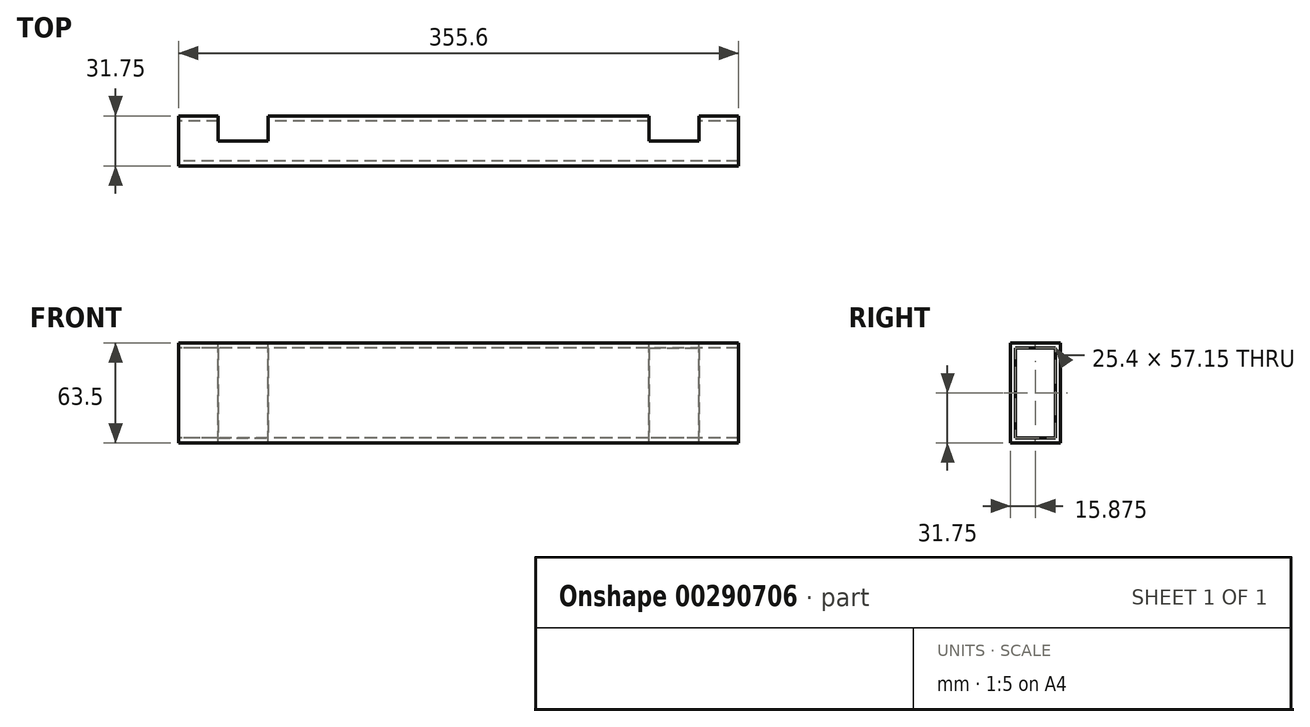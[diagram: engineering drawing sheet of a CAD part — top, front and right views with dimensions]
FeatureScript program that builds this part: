
annotation { "Feature Type Name" : "Feature", "Feature Type Description" : "" }
export const myFeature = defineFeature(function(context is Context, id is Id, definition is map)
    precondition{}
    {
        {
            var Q0;
            Q0=qCreatedBy(makeId("Front.planeOp"),FACE);
            var sketch = newSketch(context, id + "F0", { "sketchPlane" : qUnion([Q0])});
            skLineSegment(sketch, "E0.bottom", {"start": v(0, 0) * mm, "end": v(355.6, 0) * mm});
            skLineSegment(sketch, "E0.top", {"start": v(0, 63.5) * mm, "end": v(355.6, 63.5) * mm});
            skLineSegment(sketch, "E0.left", {"start": v(0, 0) * mm, "end": v(0, 63.5) * mm});
            skLineSegment(sketch, "E0.right", {"start": v(355.6, 0) * mm, "end": v(355.6, 63.5) * mm});
            skSolve(sketch);
        }
        {
            var Q0;
            Q0=makeQuery(id+"F0.imprint","IMPRINT",FACE,{"disambiguationData":[TD([[makeQuery(id+"F0.imprint","IMPRINT",EDGE,{"derivedFrom":sQuery(id+"F0.wireOp",EDGE,"E0.bottom")}),1.0]])]});
            extrude(context, id + "F1", {"entities" : qUnion([Q0]), "depth" : 31.75 * mm});
        }
        {
            var Q0;
            Q0=makeQuery(id+"F1.opExtrude","SWEPT_FACE",FACE,{"disambiguationData":[OSD([sQuery(id+"F0.wireOp",EDGE,"E0.top")])]});
            var sketch = newSketch(context, id + "F2", { "sketchPlane" : qUnion([Q0])});
            skLineSegment(sketch, "E1.bottom", {"start": v(25.19, 0) * mm, "end": v(56.94, 0) * mm});
            skLineSegment(sketch, "E1.top", {"start": v(25.19, -16.02) * mm, "end": v(56.94, -16.02) * mm});
            skLineSegment(sketch, "E1.left", {"start": v(25.19, 0) * mm, "end": v(25.19, -16.02) * mm});
            skLineSegment(sketch, "E1.right", {"start": v(56.94, 0) * mm, "end": v(56.94, -16.02) * mm});
            skLineSegment(sketch, "E2", {"start": v(177.8, 0) * mm, "end": v(177.8, -31.75) * mm, "construction": true});
            skLineSegment(sketch, "E3.MirrorCS", {"start": v(330.41, 0) * mm, "end": v(330.41, -16.02) * mm});
            skLineSegment(sketch, "E4.MirrorCS", {"start": v(330.41, -16.02) * mm, "end": v(298.66, -16.02) * mm});
            skLineSegment(sketch, "E5.MirrorCS", {"start": v(298.66, 0) * mm, "end": v(298.66, -16.02) * mm});
            skLineSegment(sketch, "E6.MirrorCS", {"start": v(330.41, 0) * mm, "end": v(298.66, 0) * mm});
            skSolve(sketch);
        }
        {
            var Q0;
            Q0=makeQuery(id+"F2.imprint","IMPRINT",FACE,{"disambiguationData":[TD([[makeQuery(id+"F2.imprint","IMPRINT",EDGE,{"derivedFrom":sQuery(id+"F2.wireOp",EDGE,"E1.bottom")}),-1.0]])]});
            var Q1;
            Q1=makeQuery(id+"F2.imprint","IMPRINT",FACE,{"disambiguationData":[TD([[makeQuery(id+"F2.imprint","IMPRINT",EDGE,{"derivedFrom":sQuery(id+"F2.wireOp",EDGE,"E3.MirrorCS")}),-1.0]])]});
            extrude(context, id + "F3", {"entities" : qUnion([Q0, Q1]), "operationType" : NewBodyOperationType.REMOVE, "endBound" : BoundingType.THROUGH_ALL, "oppositeDirection" : true, "depth" : 25.4 * mm});
        }
        {
            var Q0;
            Q0=makeQuery(id+"F1.opExtrude","SWEPT_FACE",FACE,{"disambiguationData":[OSD([sQuery(id+"F0.wireOp",EDGE,"E0.left")])]});
            var sketch = newSketch(context, id + "F4", { "sketchPlane" : qUnion([Q0])});
            skLineSegment(sketch, "E7.0", {"start": v(3.18, 60.32) * mm, "end": v(3.18, 3.18) * mm});
            skLineSegment(sketch, "E7.1", {"start": v(28.57, 60.32) * mm, "end": v(3.18, 60.32) * mm});
            skLineSegment(sketch, "E7.2", {"start": v(28.57, 3.18) * mm, "end": v(28.57, 60.32) * mm});
            skLineSegment(sketch, "E7.3", {"start": v(3.18, 3.18) * mm, "end": v(28.57, 3.18) * mm});
            skSolve(sketch);
        }
        {
            var Q0;
            Q0=makeQuery(id+"F4.imprint","IMPRINT",FACE,{"disambiguationData":[TD([[makeQuery(id+"F4.imprint","IMPRINT",EDGE,{"derivedFrom":sQuery(id+"F4.wireOp",EDGE,"E7.0")}),1.0]])]});
            extrude(context, id + "F5", {"entities" : qUnion([Q0]), "operationType" : NewBodyOperationType.REMOVE, "endBound" : BoundingType.THROUGH_ALL, "oppositeDirection" : true, "depth" : 25.4 * mm});
        }
    });
